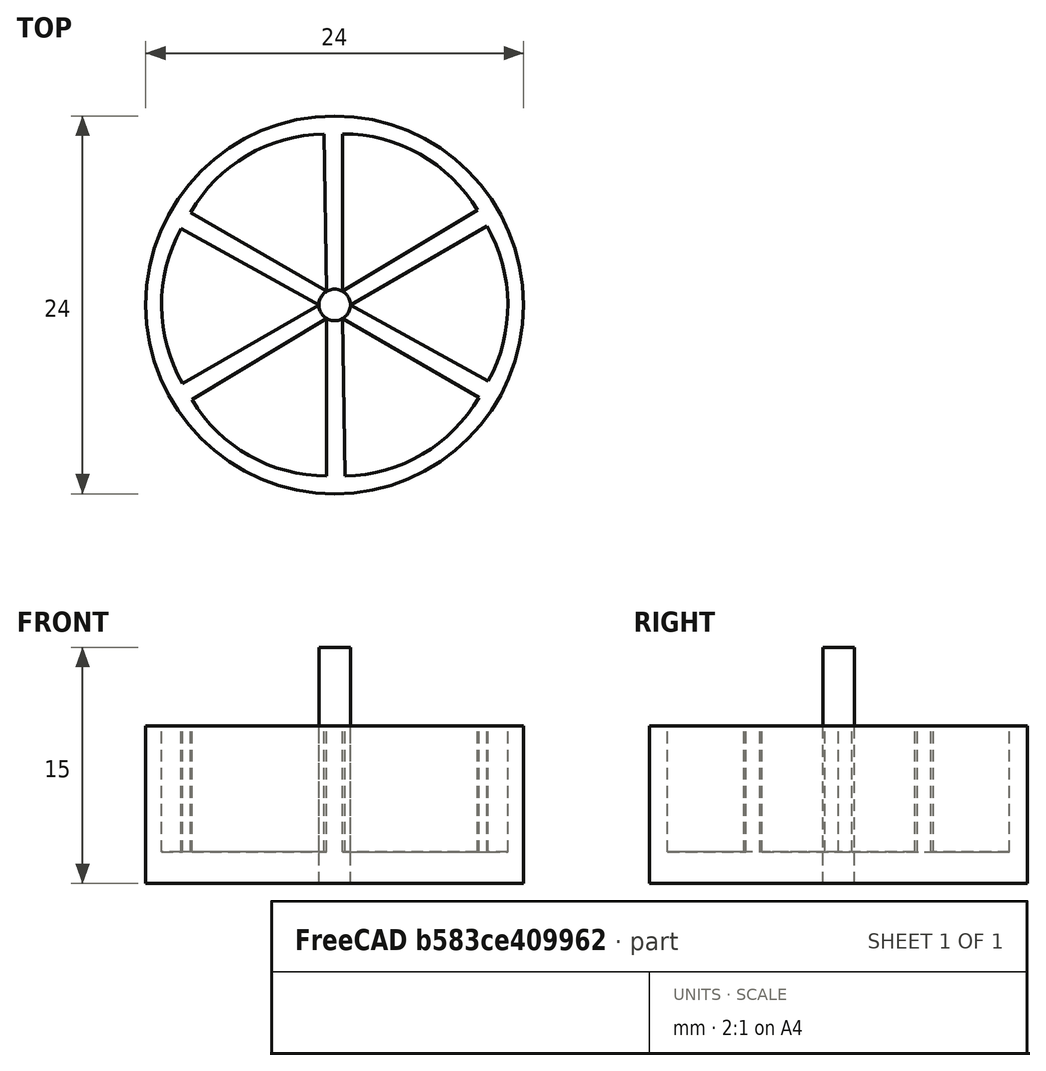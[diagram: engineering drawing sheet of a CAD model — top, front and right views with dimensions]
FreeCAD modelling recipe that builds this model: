
FCSTD DOCUMENT  (FreeCAD 0.16R6707 (Git))
Label: Caja_Trivial
License: CreativeCommons Attribution-ShareAlike
LicenseURL: http://creativecommons.org/licenses/by-sa/4.0/
objects: Part::Cylinder×3, Part::FeaturePython×1, Part::Cut×1
note: 5 computed .brp shape members not serialized (recipe doc carries the construction recipe); baked Part::Feature solids carry a one-line shape summary decoded from their .brp

FEATURE [Part::Cylinder] Cylinder  label="Caja-quesitos"
  Angle = 360
  Height = 10
  Radius = 12
FEATURE [Part::Cylinder] Cylinder001  label="Quesito"
  Angle = 59
  Height = 10
  Placement = pos=(1,0,2) rot=(0,0,-1;0.506145rad)
  Radius = 10
FEATURE [Part::Cylinder] Cylinder002  label="Referencia"
  Angle = 360
  Height = 15
  Radius = 1
FEATURE [Part::FeaturePython] Array  label="Array_quesitos"  # Draft array (typed FeaturePython)
  Angle = 360
  ArrayType = 1
  Axis = (0,0,1)
  Base = -> Cylinder001
  Center = (0,0,0)
  Fuse = false
  IntervalAxis = (0,0,0)
  IntervalX = (1,0,0)
  IntervalY = (0,1,0)
  IntervalZ = (0,0,0)
  NumberPolar = 6
  NumberX = 2
  NumberY = 2
  NumberZ = 1
FEATURE [Part::Cut] Cut
  Base = -> Cylinder
  Tool = -> Array
